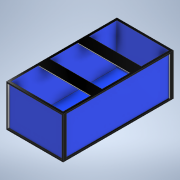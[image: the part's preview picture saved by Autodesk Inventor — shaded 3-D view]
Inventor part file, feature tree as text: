
AUTODESK INVENTOR PART (.ipt)
format: ipt  version: 2022 (Build 260153000, 153)  size: 211,456 bytes
history: native  units: in
note: dims shown in document units (in); Inventor stores cm internally (conversion verified against a paired STEP export)
features: extrude x5, sketch x5, mirror x2, other x1, pattern_linear x1
ambient origin geometry x8: Origin, YZ Plane, XZ Plane, XY Plane, X Axis, Y Axis, Z Axis, Center Point
bodies: Solid1 (feature_tree)
feature tree (14):
  other  "GlassCagesTank"
  extrude  "Extrusion1"  Depth=96.0in
  extrude  "Extrusion2"  Depth=46.5in
  extrude  "Extrusion3"  Depth=35.25in TaperAngle=0.0deg
  pattern_linear  "Rectangular Pattern1"  Spacing1=1.25in  [1 undecoded]
  extrude  "Extrusion4"  Depth=36.0in
  mirror  "Mirror2"
  mirror  "Mirror3"
  extrude  "Extrusion5"  Depth=3.0in
  sketch  "Sketch1"  dims[d0=48.0in d1=96.0in]
  sketch  "Sketch2"  dims[d2=36.0in d3=0.0in d4=46.5in]
  sketch  "Sketch3"  dims[d5=94.5in d6=35.25in d7=0.0in]
  sketch  "Sketch4"  dims[d8=50.5in]
  sketch  "Sketch5"  dims[d9=98.5in d10=1.25in d11=0.0in d12=0.7874in d14=36.0in d15=3.0in d16=2.0in d17=1.0in d18=35.0in d19=0.0in d23=1.0in d24=2.0in d25=1.0in d26=10.0in d27=10.0in d29=0.75in d30=0.0in d31=24.75in d34=24.75in d35=25.0in]
note: 1 required parameter value undecoded (feature->parameter linkage not recoverable at this tier; creation-order binding heuristic only, values carry confidence <= 0.55)
